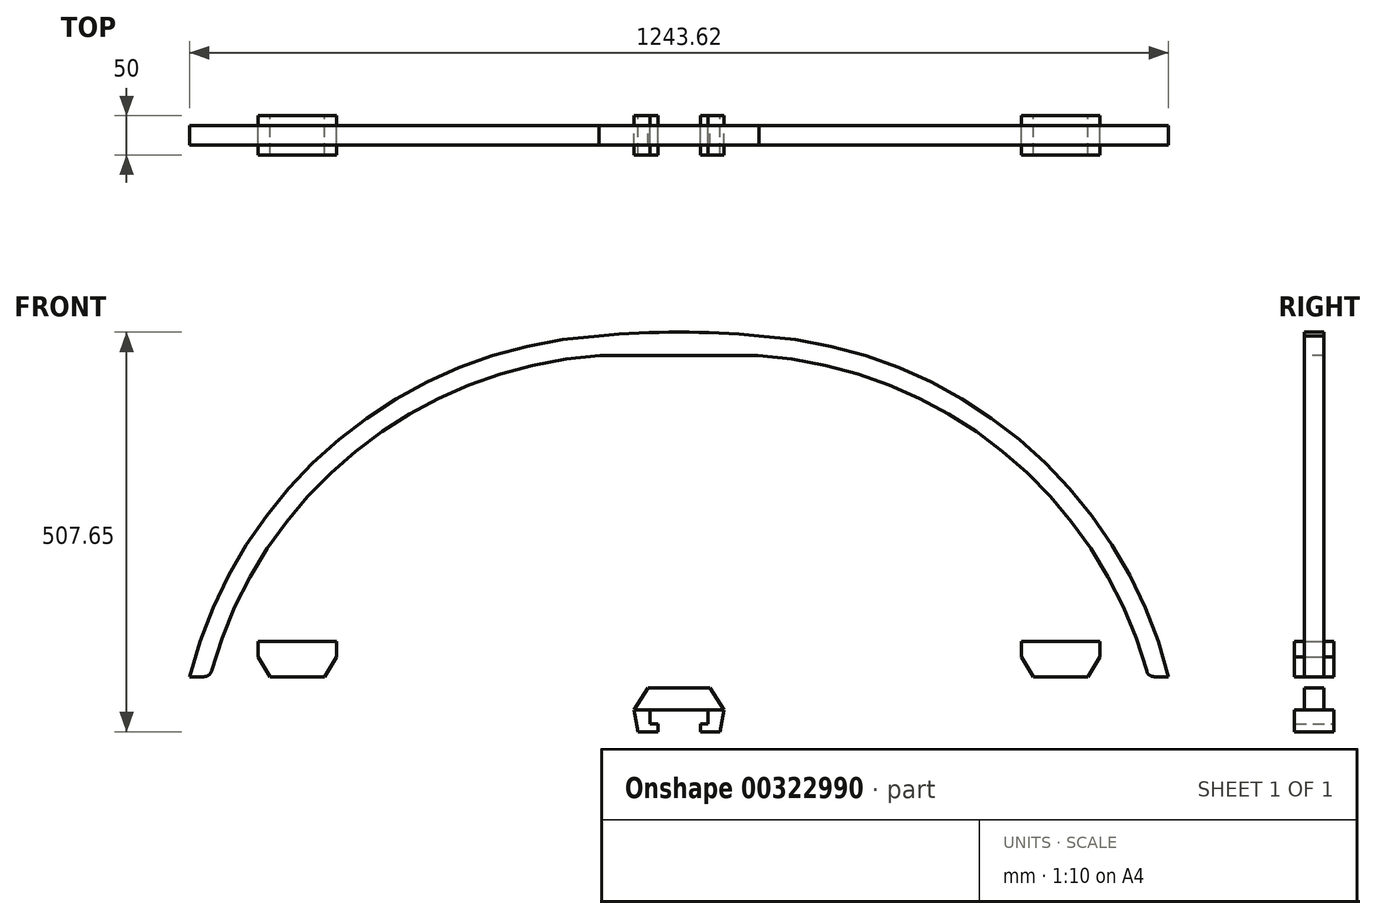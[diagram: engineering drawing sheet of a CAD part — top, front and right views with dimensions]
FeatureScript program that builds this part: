
annotation { "Feature Type Name" : "Feature", "Feature Type Description" : "" }
export const myFeature = defineFeature(function(context is Context, id is Id, definition is map)
    precondition{}
    {
        {
            var Q0;
            Q0=qCreatedBy(makeId("Front.planeOp"),FACE);
            var sketch = newSketch(context, id + "F0", { "sketchPlane" : qUnion([Q0])});
            skLineSegment(sketch, "E0.bottom", {"start": v(596, -75) * mm, "end": v(-630.77, -75) * mm});
            skLineSegment(sketch, "E0.left", {"start": v(596, -75) * mm, "end": v(596, -33) * mm});
            skPoint(sketch, "E0.middle", {"position": v(0, 0) * mm});
            skLineSegment(sketch, "E1", {"start": v(0, 0) * mm, "end": v(0, 375) * mm, "construction": true});
            skLineSegment(sketch, "E2", {"start": v(0, 0) * mm, "end": v(0, -75) * mm, "construction": true});
            skPoint(sketch, "E3.orphan", {"position": v(0, 75) * mm});
            skLineSegment(sketch, "E4", {"start": v(0, 375) * mm, "end": v(-100, 375) * mm});
            skLineSegment(sketch, "E5", {"start": v(-100, 375) * mm, "end": v(-269.87, 77.61) * mm});
            skLineSegment(sketch, "E6.MirrorCS", {"start": v(100, 375) * mm, "end": v(269.87, 77.61) * mm});
            skLineSegment(sketch, "E7.MirrorCS", {"start": v(0, 375) * mm, "end": v(100, 375) * mm});
            skPoint(sketch, "E8.orphan", {"position": v(-1634.53, 50) * mm});
            skPoint(sketch, "E9.visualSharp", {"position": v(-100, 375) * mm});
            skPoint(sketch, "E10.visualSharp", {"position": v(100, 375) * mm});
            skLineSegment(sketch, "E11", {"start": v(3.34, -47.39) * mm, "end": v(39.16, -47.39) * mm});
            skLineSegment(sketch, "E12", {"start": v(39.16, -47.39) * mm, "end": v(56.94, -75) * mm});
            skLineSegment(sketch, "E13", {"start": v(56.94, -75) * mm, "end": v(52, -103) * mm});
            skLineSegment(sketch, "E14", {"start": v(52, -103) * mm, "end": v(27, -103) * mm});
            skLineSegment(sketch, "E15", {"start": v(27, -103) * mm, "end": v(27, -93) * mm});
            skLineSegment(sketch, "E16", {"start": v(27, -93) * mm, "end": v(37, -93) * mm});
            skLineSegment(sketch, "E17", {"start": v(37, -93) * mm, "end": v(37, -75) * mm});
            skLineSegment(sketch, "E18", {"start": v(37, -75) * mm, "end": v(0, -75) * mm});
            skLineSegment(sketch, "E19.MirrorCS", {"start": v(-39.16, -47.39) * mm, "end": v(-56.94, -75) * mm});
            skLineSegment(sketch, "E20.MirrorCS", {"start": v(-37, -93) * mm, "end": v(-37, -75) * mm});
            skLineSegment(sketch, "E21.MirrorCS", {"start": v(-56.94, -75) * mm, "end": v(-52, -103) * mm});
            skLineSegment(sketch, "E22.MirrorCS", {"start": v(-52, -103) * mm, "end": v(-27, -103) * mm});
            skLineSegment(sketch, "E23.MirrorCS", {"start": v(-27, -103) * mm, "end": v(-27, -93) * mm});
            skLineSegment(sketch, "E24.MirrorCS", {"start": v(-27, -93) * mm, "end": v(-37, -93) * mm});
            skLineSegment(sketch, "E25", {"start": v(-84.48, 111.22) * mm, "end": v(-197.1, 111.22) * mm});
            skPoint(sketch, "E26.visualSharp", {"position": v(-84.64, 111.22) * mm});
            skArc(sketch, "E26.filletArc", {"start": v(-84.48, 111.22) * mm, "mid": v(-77.47, 114.08) * mm, "end": v(-74.48, 121.03) * mm});
            skLineSegment(sketch, "E27", {"start": v(0, 325) * mm, "end": v(0, 375) * mm, "construction": true});
            skLineSegment(sketch, "E28", {"start": v(-74.48, 121.03) * mm, "end": v(-71.76, 260.8) * mm});
            skLineSegment(sketch, "E29", {"start": v(-81.76, 271) * mm, "end": v(-116.4, 271) * mm});
            skLineSegment(sketch, "E30", {"start": v(-125.07, 266) * mm, "end": v(-205.77, 126.22) * mm});
            skArc(sketch, "E31.filletArc", {"start": v(-116.4, 271) * mm, "mid": v(-121.4, 269.66) * mm, "end": v(-125.07, 266) * mm});
            skArc(sketch, "E32.filletArc", {"start": v(-71.76, 260.8) * mm, "mid": v(-74.62, 268) * mm, "end": v(-81.76, 271) * mm});
            skArc(sketch, "E33.filletArc", {"start": v(-205.77, 126.22) * mm, "mid": v(-205.77, 116.22) * mm, "end": v(-197.1, 111.22) * mm});
            skLineSegment(sketch, "E34.MirrorCS", {"start": v(74.48, 121.03) * mm, "end": v(71.76, 260.8) * mm});
            skLineSegment(sketch, "E35.MirrorCS", {"start": v(81.76, 271) * mm, "end": v(116.4, 271) * mm});
            skArc(sketch, "E36.MirrorCS", {"start": v(116.4, 271) * mm, "mid": v(121.4, 269.66) * mm, "end": v(125.07, 266) * mm});
            skLineSegment(sketch, "E37.MirrorCS", {"start": v(125.07, 266) * mm, "end": v(205.77, 126.22) * mm});
            skArc(sketch, "E38.MirrorCS", {"start": v(71.76, 260.8) * mm, "mid": v(74.62, 268) * mm, "end": v(81.76, 271) * mm});
            skArc(sketch, "E39.MirrorCS", {"start": v(205.77, 126.22) * mm, "mid": v(205.77, 116.22) * mm, "end": v(197.1, 111.22) * mm});
            skLineSegment(sketch, "E40.MirrorCS", {"start": v(84.48, 111.22) * mm, "end": v(197.1, 111.22) * mm});
            skArc(sketch, "E41.MirrorCS", {"start": v(84.48, 111.22) * mm, "mid": v(77.47, 114.08) * mm, "end": v(74.48, 121.03) * mm});
            skLineSegment(sketch, "E42", {"start": v(0, 271) * mm, "end": v(0, 331) * mm, "construction": true});
            skLineSegment(sketch, "E43", {"start": v(-102.5, 331) * mm, "end": v(-102.5, 301) * mm, "construction": true});
            skCircle(sketch, "E44", {"center": v(-102.5, 301) * mm, "radius": 13 * mm});
            skLineSegment(sketch, "E45", {"start": v(-102.5, 301) * mm, "end": v(-102.5, 25.54) * mm, "construction": true});
            skPoint(sketch, "E46", {"position": v(-102.5, 63) * mm});
            skCircle(sketch, "E47", {"center": v(-102.5, 63) * mm, "radius": 13 * mm});
            skCircle(sketch, "E48.MirrorC", {"center": v(102.5, 301) * mm, "radius": 13 * mm});
            skCircle(sketch, "E49.MirrorC", {"center": v(102.5, 63) * mm, "radius": 13 * mm});
            skLineSegment(sketch, "E50", {"start": v(0, 375) * mm, "end": v(0, 355) * mm, "construction": true});
            skPoint(sketch, "E51", {"position": v(-52.33, 355) * mm});
            skPoint(sketch, "E52", {"position": v(60, 355) * mm});
            skCircle(sketch, "E53", {"center": v(102.5, 301) * mm, "radius": 18 * mm});
            skCircle(sketch, "E54", {"center": v(-102.5, 301) * mm, "radius": 18 * mm});
            skCircle(sketch, "E55", {"center": v(-102.5, 63) * mm, "radius": 18 * mm});
            skCircle(sketch, "E56", {"center": v(102.5, 63) * mm, "radius": 18 * mm});
            skLineSegment(sketch, "E57", {"start": v(-39.16, -47.39) * mm, "end": v(3.34, -47.39) * mm});
            skLineSegment(sketch, "E58", {"start": v(-37, -103) * mm, "end": v(-37, -33) * mm, "construction": true});
            skPoint(sketch, "E59", {"position": v(-450, -33) * mm});
            skArc(sketch, "E60", {"start": v(-450, -33) * mm, "mid": v(-345.78, -0.75) * mm, "end": v(-269.87, 77.61) * mm});
            skLineSegment(sketch, "E61.MirrorCS", {"start": v(-534.8, -8) * mm, "end": v(-534.8, 12) * mm});
            skLineSegment(sketch, "E62.MirrorCS", {"start": v(-534.8, 12) * mm, "end": v(-484.8, 12) * mm});
            skLineSegment(sketch, "E63.MirrorCS", {"start": v(-434.8, 12) * mm, "end": v(-484.8, 12) * mm});
            skLineSegment(sketch, "E64.MirrorCS", {"start": v(-434.8, -8) * mm, "end": v(-434.8, 12) * mm});
            skLineSegment(sketch, "E65.MirrorCS", {"start": v(-484.8, -33) * mm, "end": v(-449.23, -33) * mm});
            skLineSegment(sketch, "E66", {"start": v(-434.8, -8) * mm, "end": v(-450, -33) * mm});
            skLineSegment(sketch, "E67", {"start": v(-484.8, 18.96) * mm, "end": v(-484.8, -38.61) * mm, "construction": true});
            skLineSegment(sketch, "E68.MirrorCS", {"start": v(-534.8, -8) * mm, "end": v(-519.58, -33) * mm});
            skLineSegment(sketch, "E69", {"start": v(-596, -75) * mm, "end": v(-596, -33) * mm});
            skArc(sketch, "E70", {"start": v(-100, 375) * mm, "mid": v(-413.73, 250.91) * mm, "end": v(-596, -33) * mm});
            skArc(sketch, "E71.0", {"start": v(-101.62, 399.95) * mm, "mid": v(-448.4, 254.07) * mm, "end": v(-630.77, -75) * mm});
            skArc(sketch, "E72.MirrorCS", {"start": v(100, 375) * mm, "mid": v(413.73, 250.91) * mm, "end": v(596, -33) * mm});
            skArc(sketch, "E73.MirrorCS", {"start": v(101.62, 399.95) * mm, "mid": v(448.4, 254.07) * mm, "end": v(630.77, -75) * mm});
            skArc(sketch, "E74", {"start": v(101.62, 399.95) * mm, "mid": v(0, 404.65) * mm, "end": v(-101.62, 399.95) * mm});
            skLineSegment(sketch, "E75.MirrorCS", {"start": v(-596, -75) * mm, "end": v(630.77, -75) * mm});
            skLineSegment(sketch, "E76.MirrorCS", {"start": v(450, -33) * mm, "end": v(621.81, -33) * mm});
            skLineSegment(sketch, "E77.MirrorCS", {"start": v(434.8, -8) * mm, "end": v(450, -33) * mm});
            skLineSegment(sketch, "E78.MirrorCS", {"start": v(534.8, 12) * mm, "end": v(484.8, 12) * mm});
            skLineSegment(sketch, "E79.MirrorCS", {"start": v(434.8, -8) * mm, "end": v(434.8, 12) * mm});
            skLineSegment(sketch, "E80.MirrorCS", {"start": v(534.8, -8) * mm, "end": v(519.58, -33) * mm});
            skLineSegment(sketch, "E81.MirrorCS", {"start": v(484.8, 18.96) * mm, "end": v(484.8, -38.61) * mm, "construction": true});
            skLineSegment(sketch, "E82.MirrorCS", {"start": v(434.8, 12) * mm, "end": v(484.8, 12) * mm});
            skLineSegment(sketch, "E83.MirrorCS", {"start": v(534.8, -8) * mm, "end": v(534.8, 12) * mm});
            skLineSegment(sketch, "E84.trimOffspring", {"start": v(-449.23, -33) * mm, "end": v(-621.81, -33) * mm});
            skArc(sketch, "E85.MirrorCS", {"start": v(450, -33) * mm, "mid": v(345.78, -0.75) * mm, "end": v(269.87, 77.61) * mm});
            skPoint(sketch, "E86.orphan", {"position": v(37, -33) * mm});
            skSolve(sketch);
        }
        {
            var Q0;
            {var subQ8=sQuery(id+"F0.wireOp",EDGE,"E5");Q0=makeQuery(id+"F0.imprint","IMPRINT",FACE,{"disambiguationData":[TD([[makeQuery(id+"F0.imprint","IMPRINT",EDGE,{"derivedFrom":subQ8}),1.0]])]});}
            var Q1;
            {var subQ12=sQuery(id+"F0.wireOp",EDGE,"E70");Q1=makeQuery(id+"F0.imprint","IMPRINT",FACE,{"disambiguationData":[TD([[makeQuery(id+"F0.imprint","IMPRINT",EDGE,{"derivedFrom":subQ12}),-1.0]])]});}
            var Q2;
            {var subQ0=sQuery(id+"F0.wireOp",EDGE,"E0.bottom");Q2=makeQuery(id+"F0.imprint","IMPRINT",FACE,{"disambiguationData":[TD([[makeQuery(id+"F0.imprint","IMPRINT",EDGE,{"derivedFrom":subQ0}),-1.0]])]});}
            var Q3;
            {var subQ5=sQuery(id+"F0.wireOp",EDGE,"E0.left");Q3=makeQuery(id+"F0.imprint","IMPRINT",FACE,{"disambiguationData":[TD([[makeQuery(id+"F0.imprint","IMPRINT",EDGE,{"derivedFrom":subQ5}),-1.0]])]});}
            var Q4;
            {var subQ0=sQuery(id+"F0.wireOp",EDGE,"e67435ad-6dde-46e6-a052-0d0444990060.converted");var subQ1=makeQuery(id+"F0.imprint","INTERSECT",VERTEX,{"derivedFrom":[sQuery(id+"F0.wireOp",EDGE,"E5"),subQ0]});Q4=makeQuery(id+"F0.imprint","IMPRINT",FACE,{"disambiguationData":[TD([[makeQuery(id+"F0.imprint","IMPRINT",EDGE,{"disambiguationData":[TD([[subQ1,1.0]])],"derivedFrom":subQ0}),1.0]])]});}
            extrude(context, id + "F1", {"entities" : qUnion([Q0, Q1, Q2, Q3, Q4]), "depth" : 25 * mm, "symmetric" : true});
        }
        {
            var Q0;
            Q0=makeQuery(id+"F1.opExtrude","SWEPT_EDGE",EDGE,{"disambiguationData":[OSD([sQuery(id+"F0.wireOp",EDGE,"E4"),sQuery(id+"F0.wireOp",EDGE,"E5"),sQuery(id+"F0.wireOp",EDGE,"E70")])]});
            var Q1;
            Q1=makeQuery(id+"F1.opExtrude","SWEPT_EDGE",EDGE,{"disambiguationData":[OSD([sQuery(id+"F0.wireOp",EDGE,"E6.MirrorCS"),sQuery(id+"F0.wireOp",EDGE,"E7.MirrorCS"),sQuery(id+"F0.wireOp",EDGE,"E72.MirrorCS")])]});
            var Q2;
            Q2=makeQuery(id+"F1.opExtrude","SWEPT_EDGE",EDGE,{"disambiguationData":[OSD([sQuery(id+"F0.wireOp",EDGE,"E72.MirrorCS"),sQuery(id+"F0.wireOp",EDGE,"E0.left"),sQuery(id+"F0.wireOp",EDGE,"E76.MirrorCS")])]});
            var Q3;
            Q3=makeQuery(id+"F1.opExtrude","SWEPT_EDGE",EDGE,{"disambiguationData":[OSD([sQuery(id+"F0.wireOp",EDGE,"E69"),sQuery(id+"F0.wireOp",EDGE,"E70"),sQuery(id+"F0.wireOp",EDGE,"E84.trimOffspring")])]});
            fillet(context, id + "F2", {"entities" : qUnion([Q0, Q1, Q2, Q3]), "radius" : 10 * mm, "tangentPropagation" : true, "allowEdgeOverflow" : false});
        }
        {
            var Q0;
            Q0=makeQuery(id+"F0.imprint","IMPRINT",FACE,{"disambiguationData":[TD([[makeQuery(id+"F0.imprint","IMPRINT",EDGE,{"derivedFrom":sQuery(id+"F0.wireOp",EDGE,"E61.MirrorCS")}),-1.0]])]});
            var Q1;
            Q1=makeQuery(id+"F0.imprint","IMPRINT",FACE,{"disambiguationData":[TD([[makeQuery(id+"F0.imprint","IMPRINT",EDGE,{"derivedFrom":sQuery(id+"F0.wireOp",EDGE,"E11")}),-1.0]])]});
            var Q2;
            {var subQ0=sQuery(id+"F0.wireOp",EDGE,"E13");Q2=makeQuery(id+"F0.imprint","IMPRINT",FACE,{"disambiguationData":[TD([[makeQuery(id+"F0.imprint","IMPRINT",EDGE,{"derivedFrom":subQ0}),-1.0]])]});}
            var Q3;
            {var subQ2=sQuery(id+"F0.wireOp",EDGE,"E20.MirrorCS");Q3=makeQuery(id+"F0.imprint","IMPRINT",FACE,{"disambiguationData":[TD([[makeQuery(id+"F0.imprint","IMPRINT",EDGE,{"derivedFrom":subQ2}),1.0]])]});}
            var Q4;
            Q4=makeQuery(id+"F0.imprint","IMPRINT",FACE,{"disambiguationData":[TD([[makeQuery(id+"F0.imprint","IMPRINT",EDGE,{"derivedFrom":sQuery(id+"F0.wireOp",EDGE,"E78.MirrorCS")}),1.0]])]});
            extrude(context, id + "F3", {"entities" : qUnion([Q0, Q1, Q2, Q3, Q4]), "operationType" : NewBodyOperationType.ADD, "depth" : 50 * mm, "symmetric" : true});
        }
    });
